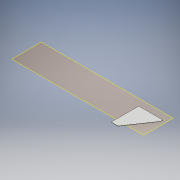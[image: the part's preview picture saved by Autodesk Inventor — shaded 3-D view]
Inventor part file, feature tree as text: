
AUTODESK INVENTOR PART (.ipt)
format: ipt  version: 2018 (Build 220112000, 112)  size: 120,832 bytes
history: native  units: mm
features: other x5, plane x1, sheet_metal_op x1, sketch x1
ambient origin geometry x8: Origin, YZ Plane, XZ Plane, XY Plane, X Axis, Y Axis, Z Axis, Center Point
bodies: Solid1 (feature_tree)
feature tree (8):
  plane  "Work Plane1"
  sheet_metal_op  "Face1"
  sketch  "Sketch1"  dims[d0=9.721484mm d1=2.0mm d2=200.0mm d3=20.0mm d4=230.0mm]
  other  "Plate1"
  other  "Definition1"
  parser-record x1  (decoder bookkeeping rows leaked as tree rows — omitted from the tree; the rows remain in map.json)
  other  "svejselære.iam"
  other  "plade:1"
note: 1 file-system path scrubbed to <path> (originals preserved in map.json)
